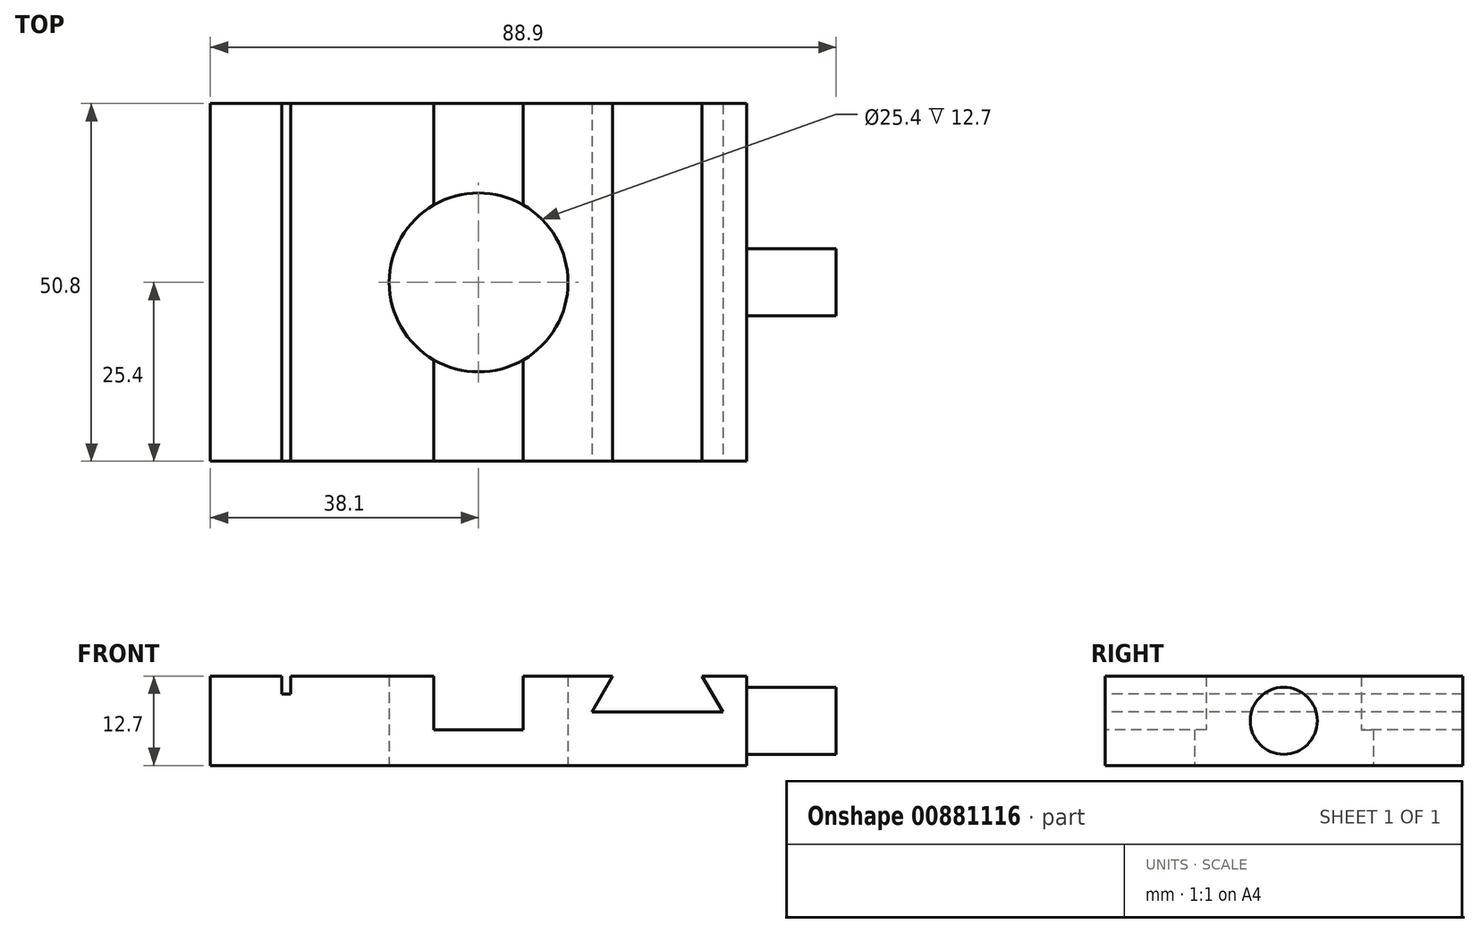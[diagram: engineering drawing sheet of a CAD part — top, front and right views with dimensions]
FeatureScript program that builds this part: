
annotation { "Feature Type Name" : "Feature", "Feature Type Description" : "" }
export const myFeature = defineFeature(function(context is Context, id is Id, definition is map)
    precondition{}
    {
        {
            var Q0;
            Q0=qCreatedBy(makeId("Top.planeOp"),FACE);
            var sketch = newSketch(context, id + "F0", { "sketchPlane" : qUnion([Q0])});
            skLineSegment(sketch, "E0.bottom", {"start": v(38.1, -25.4) * mm, "end": v(-38.1, -25.4) * mm});
            skLineSegment(sketch, "E0.top", {"start": v(38.1, 25.4) * mm, "end": v(-38.1, 25.4) * mm});
            skLineSegment(sketch, "E0.left", {"start": v(38.1, -25.4) * mm, "end": v(38.1, 25.4) * mm});
            skLineSegment(sketch, "E0.right", {"start": v(-38.1, -25.4) * mm, "end": v(-38.1, 25.4) * mm});
            skPoint(sketch, "E0.middle", {"position": v(0, 0) * mm});
            skCircle(sketch, "E1", {"center": v(0, 0) * mm, "radius": 12.7 * mm});
            skSolve(sketch);
        }
        {
            var Q0;
            Q0=makeQuery(id+"F0.imprint","IMPRINT",FACE,{"disambiguationData":[TD([[makeQuery(id+"F0.imprint","IMPRINT",EDGE,{"derivedFrom":sQuery(id+"F0.wireOp",EDGE,"E0.bottom")}),-1.0]])]});
            extrude(context, id + "F1", {"entities" : qUnion([Q0]), "depth" : 12.7 * mm, "offsetDistance" : 25 * mm});
        }
        {
            var Q0;
            Q0=makeQuery(id+"F1.opExtrude","SWEPT_FACE",FACE,{"disambiguationData":[OSD([sQuery(id+"F0.wireOp",EDGE,"E0.bottom")])]});
            var sketch = newSketch(context, id + "F2", { "sketchPlane" : qUnion([Q0])});
            skLineSegment(sketch, "E2.bottom", {"start": v(-27.94, 12.7) * mm, "end": v(-26.67, 12.7) * mm});
            skLineSegment(sketch, "E2.top", {"start": v(-27.94, 12.7) * mm, "end": v(-26.67, 12.7) * mm});
            skLineSegment(sketch, "E2.left", {"start": v(-27.94, 12.7) * mm, "end": v(-27.94, 12.7) * mm});
            skLineSegment(sketch, "E2.right", {"start": v(-26.67, 12.7) * mm, "end": v(-26.67, 12.7) * mm});
            skLineSegment(sketch, "E3.bottom", {"start": v(-6.35, 12.7) * mm, "end": v(6.35, 12.7) * mm});
            skLineSegment(sketch, "E3.top", {"start": v(-6.35, 12.7) * mm, "end": v(6.35, 12.7) * mm});
            skLineSegment(sketch, "E3.left", {"start": v(-6.35, 12.7) * mm, "end": v(-6.35, 12.7) * mm});
            skLineSegment(sketch, "E3.right", {"start": v(6.35, 12.7) * mm, "end": v(6.35, 12.7) * mm});
            skPoint(sketch, "E4", {"position": v(0, 0) * mm});
            skLineSegment(sketch, "E5", {"start": v(0, 12.7) * mm, "end": v(0, 12.7) * mm});
            skLineSegment(sketch, "E6.top", {"start": v(-27.94, 10.16) * mm, "end": v(-26.67, 10.16) * mm});
            skLineSegment(sketch, "E6.left", {"start": v(-27.94, 12.7) * mm, "end": v(-27.94, 10.16) * mm});
            skLineSegment(sketch, "E6.right", {"start": v(-26.67, 12.7) * mm, "end": v(-26.67, 10.16) * mm});
            skLineSegment(sketch, "E7.top", {"start": v(-6.35, 5.08) * mm, "end": v(6.35, 5.08) * mm});
            skLineSegment(sketch, "E7.left", {"start": v(-6.35, 12.7) * mm, "end": v(-6.35, 5.08) * mm});
            skLineSegment(sketch, "E7.right", {"start": v(6.35, 12.7) * mm, "end": v(6.35, 5.08) * mm});
            skSolve(sketch);
        }
        {
            var Q0;
            Q0=makeQuery(id+"F2.imprint","IMPRINT",FACE,{"disambiguationData":[TD([[makeQuery(id+"F2.imprint","IMPRINT",EDGE,{"derivedFrom":sQuery(id+"F2.wireOp",EDGE,"E6.top")}),-1.0]])]});
            extrude(context, id + "F3", {"entities" : qUnion([Q0]), "operationType" : NewBodyOperationType.INTERSECT, "endBound" : BoundingType.THROUGH_ALL, "oppositeDirection" : true, "depth" : 5.08 * mm, "offsetDistance" : 25.4 * mm});
        }
        {
            var Q0;
            Q0=makeQuery(id+"F1.opExtrude","SWEPT_FACE",FACE,{"disambiguationData":[OSD([sQuery(id+"F0.wireOp",EDGE,"E0.bottom")])]});
            var sketch = newSketch(context, id + "F4", { "sketchPlane" : qUnion([Q0])});
            skLineSegment(sketch, "E8", {"start": v(19.05, 12.7) * mm, "end": v(16.12, 7.62) * mm});
            skLineSegment(sketch, "E9", {"start": v(16.12, 7.62) * mm, "end": v(34.68, 7.62) * mm});
            skLineSegment(sketch, "E10", {"start": v(34.68, 7.62) * mm, "end": v(31.75, 12.7) * mm});
            skLineSegment(sketch, "E11", {"start": v(31.75, 12.7) * mm, "end": v(19.05, 12.7) * mm});
            skLineSegment(sketch, "E12", {"start": v(25.4, 12.7) * mm, "end": v(25.4, 7.62) * mm, "construction": true});
            skSolve(sketch);
        }
        {
            var Q0;
            Q0=makeQuery(id+"F4.imprint","IMPRINT",FACE,{"disambiguationData":[TD([[makeQuery(id+"F4.imprint","IMPRINT",EDGE,{"derivedFrom":sQuery(id+"F4.wireOp",EDGE,"E8")}),1.0]])]});
            extrude(context, id + "F5", {"entities" : qUnion([Q0]), "operationType" : NewBodyOperationType.REMOVE, "endBound" : BoundingType.THROUGH_ALL, "oppositeDirection" : true, "depth" : 25.4 * mm, "offsetDistance" : 25.4 * mm});
        }
        {
            var Q0;
            Q0=makeQuery(id+"F1.opExtrude","SWEPT_FACE",FACE,{"disambiguationData":[OSD([sQuery(id+"F0.wireOp",EDGE,"E0.left")])]});
            var sketch = newSketch(context, id + "F6", { "sketchPlane" : qUnion([Q0])});
            skCircle(sketch, "E13", {"center": v(0, 6.35) * mm, "radius": 4.76 * mm});
            skPoint(sketch, "E13.centerSnap0", {"position": v(-25.4, 6.35) * mm});
            skPoint(sketch, "E13.centerSnap1", {"position": v(0, 12.7) * mm});
            skSolve(sketch);
        }
        {
            var Q0;
            Q0=makeQuery(id+"F6.imprint","IMPRINT",FACE,{"disambiguationData":[TD([[makeQuery(id+"F6.imprint","IMPRINT",EDGE,{"derivedFrom":sQuery(id+"F6.wireOp",EDGE,"E13")}),1.0]])]});
            extrude(context, id + "F7", {"entities" : qUnion([Q0]), "operationType" : NewBodyOperationType.ADD, "depth" : 12.7 * mm, "offsetDistance" : 25.4 * mm});
        }
    });
